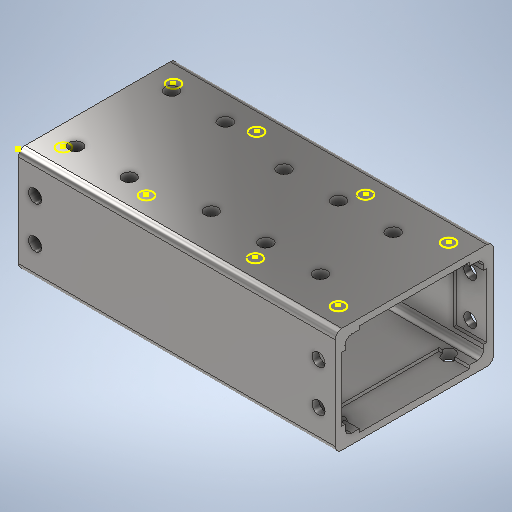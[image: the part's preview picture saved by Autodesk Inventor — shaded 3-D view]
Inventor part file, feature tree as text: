
AUTODESK INVENTOR PART (.ipt)
format: ipt  version: 2025.2 (Build 292293000, 293)  size: 399,872 bytes
history: native  units: in
note: dims shown in document units (in); Inventor stores cm internally (conversion verified against a paired STEP export)
features: extrude x6, mirror x2, sketch x2, projected_geometry x2, shell x1, fillet x1, plane x1
ambient origin geometry x8: Origin, YZ Plane, XZ Plane, XY Plane, X Axis, Y Axis, Z Axis, Center Point
bodies: Solid1 (feature_tree)
feature tree (15):
  extrude  "Extrusion1"  Depth=2.0in
  shell  "Shell1"  Thickness=6.0in
  fillet  "Fillet1"  Radius=0.1875in
  plane  "Work Plane1"
  extrude  "Extrusion2"  Depth=0.5768in
  mirror  "Mirror1"
  extrude  "Extrusion3"  Depth=2.0866in
  extrude  "Extrusion4"  Depth=0.5768in
  extrude  "Extrusion5"  Depth=0.3937in
  mirror  "Mirror2"
  extrude  "Extrusion6"  Depth=6.0in TaperAngle=0.0deg
  sketch  "Sketch8"  dims[d5=0.125in d6=0.2362in d7=2.0866in d8=1.5748in d9=0.3937in d10=6.0in d11=0.0in d12=0.25in d13=2.0in d14=3.0in d16=0.5906in d17=0.4921in d18=1.0in d19=0.0in d20=4.0in d21=3.0in d22=2.0in d23=2.5in d24=0.25in d25=0.25in d27=0.5906in d28=1.0in d29=0.0in d31=3.5in d32=2.0in d33=0.6299in d34=0.25in d35=0.7874in d36=0.0in d37=0.0in d38=1.0in d39=2.75in d40=1.75in d41=1.5in d42=1.2126in d43=2.0866in d44=0.5768in d45=0.0in d46=1.378in]
  sketch  "Sketch7"  dims[d0=3.0in d1=2.0in d2=6.0in d3=0.0in d4=0.1875in]
  projected_geometry  "Projected Loop1"
  projected_geometry  "Projected Loop2"
